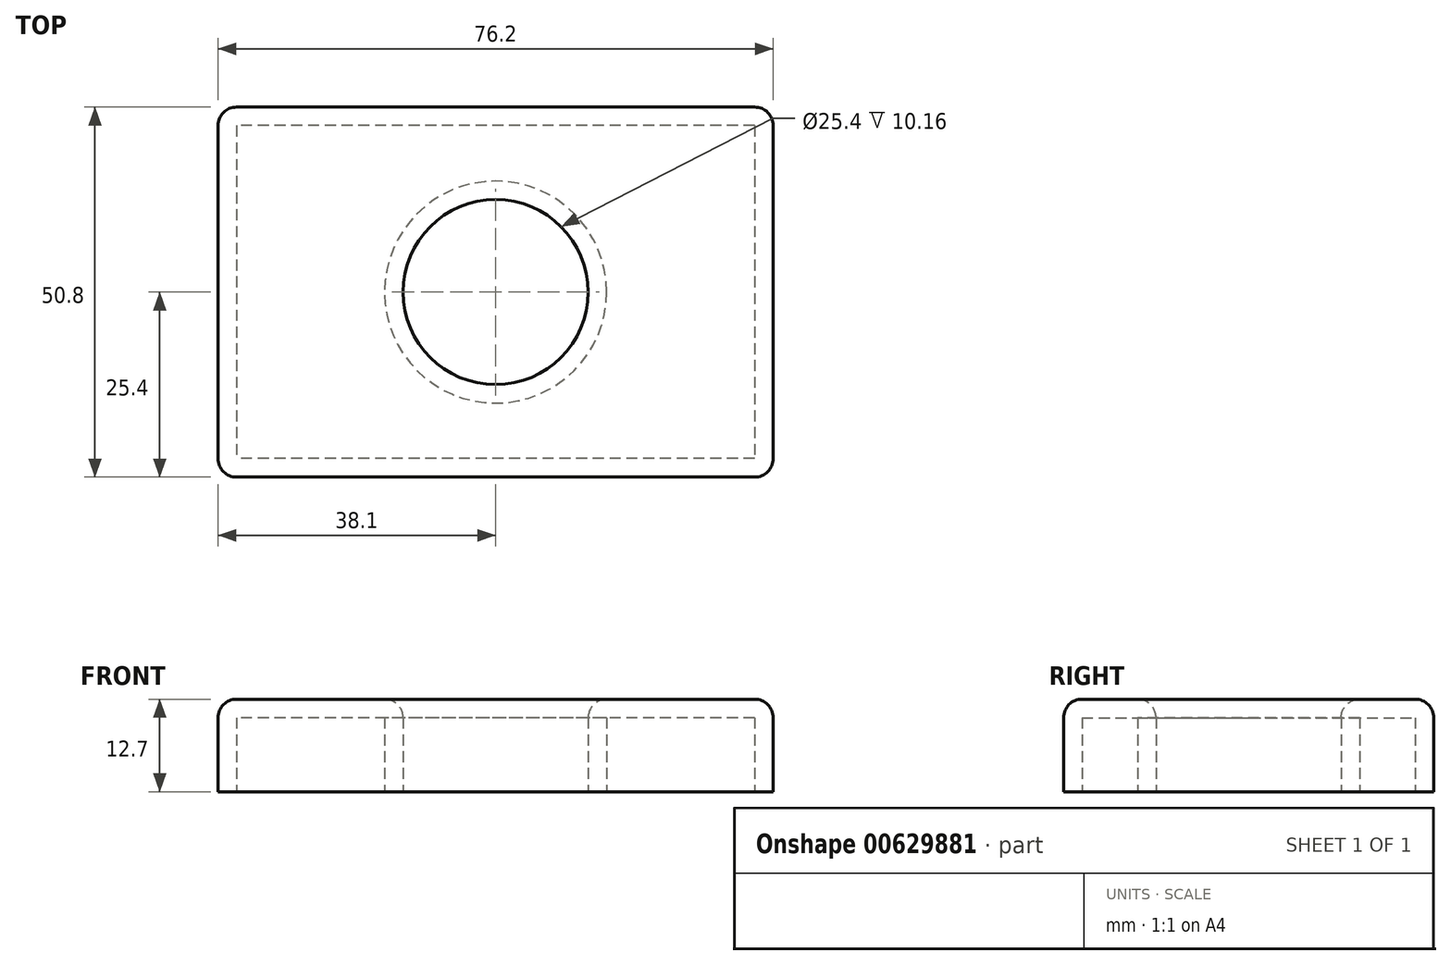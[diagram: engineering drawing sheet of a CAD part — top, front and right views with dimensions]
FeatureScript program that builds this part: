
annotation { "Feature Type Name" : "Feature", "Feature Type Description" : "" }
export const myFeature = defineFeature(function(context is Context, id is Id, definition is map)
    precondition{}
    {
        {
            var Q0;
            Q0=qCreatedBy(makeId("Top.planeOp"),FACE);
            var sketch = newSketch(context, id + "F0", { "sketchPlane" : qUnion([Q0])});
            skLineSegment(sketch, "E0.bottom", {"start": v(38.1, 25.4) * mm, "end": v(-38.1, 25.4) * mm});
            skLineSegment(sketch, "E0.top", {"start": v(38.1, -25.4) * mm, "end": v(-38.1, -25.4) * mm});
            skLineSegment(sketch, "E0.left", {"start": v(38.1, 25.4) * mm, "end": v(38.1, -25.4) * mm});
            skLineSegment(sketch, "E0.right", {"start": v(-38.1, 25.4) * mm, "end": v(-38.1, -25.4) * mm});
            skPoint(sketch, "E0.middle", {"position": v(0, 0) * mm});
            skCircle(sketch, "E1", {"center": v(0, 0) * mm, "radius": 12.7 * mm});
            skSolve(sketch);
        }
        {
            var Q0;
            Q0=makeQuery(id+"F0.imprint","IMPRINT",FACE,{"disambiguationData":[TD([[makeQuery(id+"F0.imprint","IMPRINT",EDGE,{"derivedFrom":sQuery(id+"F0.wireOp",EDGE,"E0.bottom")}),1.0]])]});
            extrude(context, id + "F1", {"entities" : qUnion([Q0]), "depth" : 12.7 * mm, "offsetDistance" : 25.4 * mm});
        }
        {
            var Q0;
            Q0=makeQuery(id+"F1.opExtrude","SWEPT_EDGE",EDGE,{"disambiguationData":[OSD([sQuery(id+"F0.wireOp",EDGE,"E0.top"),sQuery(id+"F0.wireOp",EDGE,"E0.right")])]});
            var Q1;
            Q1=makeQuery(id+"F1.opExtrude","SWEPT_EDGE",EDGE,{"disambiguationData":[OSD([sQuery(id+"F0.wireOp",EDGE,"E0.top"),sQuery(id+"F0.wireOp",EDGE,"E0.left")])]});
            var Q2;
            Q2=makeQuery(id+"F1.opExtrude","SWEPT_EDGE",EDGE,{"disambiguationData":[OSD([sQuery(id+"F0.wireOp",EDGE,"E0.bottom"),sQuery(id+"F0.wireOp",EDGE,"E0.left")])]});
            var Q3;
            Q3=makeQuery(id+"F1.opExtrude","SWEPT_EDGE",EDGE,{"disambiguationData":[OSD([sQuery(id+"F0.wireOp",EDGE,"E0.bottom"),sQuery(id+"F0.wireOp",EDGE,"E0.right")])]});
            var Q4;
            Q4=makeQuery(id+"F1.opExtrude","CAP_EDGE",EDGE,{"disambiguationData":[OSD([sQuery(id+"F0.wireOp",EDGE,"E0.bottom")])],"isStart":false});
            var Q5;
            Q5=makeQuery(id+"F1.opExtrude","CAP_EDGE",EDGE,{"disambiguationData":[OSD([sQuery(id+"F0.wireOp",EDGE,"E0.right")])],"isStart":false});
            var Q6;
            Q6=makeQuery(id+"F1.opExtrude","CAP_EDGE",EDGE,{"disambiguationData":[OSD([sQuery(id+"F0.wireOp",EDGE,"E0.top")])],"isStart":false});
            var Q7;
            Q7=makeQuery(id+"F1.opExtrude","CAP_EDGE",EDGE,{"disambiguationData":[OSD([sQuery(id+"F0.wireOp",EDGE,"E0.left")])],"isStart":false});
            var Q8;
            Q8=makeQuery(id+"F1.opExtrude","CAP_EDGE",EDGE,{"disambiguationData":[OSD([sQuery(id+"F0.wireOp",EDGE,"E1")])],"isStart":false});
            fillet(context, id + "F2", {"entities" : qUnion([Q0, Q1, Q2, Q3, Q4, Q5, Q6, Q7, Q8]), "radius" : 2.54 * mm, "tangentPropagation" : true, "allowEdgeOverflow" : false});
        }
        {
            var Q0;
            Q0=makeQuery(id+"F1.opExtrude","CAP_FACE",FACE,{"disambiguationData":[OSD([sQuery(id+"F0.wireOp",EDGE,"E0.bottom"),sQuery(id+"F0.wireOp",EDGE,"E0.top"),sQuery(id+"F0.wireOp",EDGE,"E0.left"),sQuery(id+"F0.wireOp",EDGE,"E0.right"),sQuery(id+"F0.wireOp",EDGE,"E1")])],"isStart":true});
            shell(context, id + "F3", {"entities" : qUnion([Q0]), "thickness" : 2.54 * mm});
        }
    });
